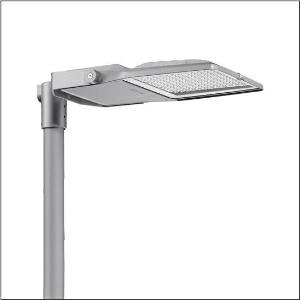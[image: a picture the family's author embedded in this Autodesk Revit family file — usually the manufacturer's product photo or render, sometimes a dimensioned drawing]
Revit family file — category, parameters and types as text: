
# Revit family: floodlight_fl_21_iq_midi___pl64_5xa7782f2e3a_4586
name_source: partatom
category: Lighting Fixtures
units: mm (PartAtom-declared; Revit-internal decimal feet)

## family parameters
Cut with Voids When Loaded = No
Host = Face
Light Source = No
Part Type = Normal
Room Calculation Point = No
Round Connector Dimension = Use Diameter
Shared = No

## types (1)
- --- (1 x LED, 34530 lm, 270.2 W, 3000K)
    Apparent Load = 270 VA
    CIE Flux Codes = 28 80 98 100 100
    Color Rendering = 70
    Color Temperature = 3000K
    Default Elevation = 1800 mm
    Description = Floodlight FL 21 iQ midi, floodlight, primary light control with lens, of PMMA, primary optical cover: protective disc, of toughened safety glass, transparent, light distribution: PL64, light emission: direct distribution, installation type: surface-mounted, LED, High Power LED, rated luminous flux: 34.530lm, luminous efficacy: 128lm/W, light colour: 730, colour temperature: 3000K, control gear: ECG iQ, control: optimised constant luminous flux control (CLO 2.0), Desk-Remote (wireless, voltage-free reading and setting of iQ features in the workshop via application-optimized NFC function/RFID function), Smart-Wire, Night-Set, Temp-Guard, Auto-Match, Street-Remote, with terminal, 6-pole, mains connection: 220..240V, AC, 50/60Hz, start of lifetime: 270W, end of service life: 287W, reduction: 117W, luminaire housing, of diecast aluminium, powder-coated, Siteco® metallic grey (DB 702S), corrosivity category C5 mid according to DIN EN ISO 12944, sealing non-destructively replaceable, please order mast flange separately, mast bracket, of steel, galvanised, powder-coated, Siteco® metallic grey (DB 702S), protection rating (complete): IP66, insulation class (complete): insulation class II (safety insulation), certification: CE, protection symbol: D, impact resistance: IK08, permissible operating ambient temperature: -40..+40°C, permissible operating ambient temperature for outdoor applications: -40..+50°C, standard: DIN EN 12944, LABS conformity tested according to VDMA 24364:2018-05, packaging unit: 1 piece

Light Distribution: PL64
    Height = 76 mm
    Lamp = 1 x LED
    Lamp Light Flux = 34530 lm
    Lamp Power = 270.2 W
    Lamp count = 1
    Length = 657 mm
    Luminous efficacy = 128 lm/W
    Manufacturer = Siteco
    ModVariant = No
    Model = 5XA7782F2E3A
    Number of Poles = 1
    OnlyDefault = Yes
    Power Factor = 1
    Product Name = Floodlight FL 21 iQ midi | PL64
    Product group = floodlight | pylon annexe
    ProductGroupID = 6200
    Protection Class = Protection class II
    Protection Degree = IP 66
    RLX_Detail_Level = 1
    RLX_Emergency_Light_Flux = 0 lm
    RLX_Emergency_Type = 0
    RLX_Emergency_Type_DB = No
    RlxData = <blob elided: 153677 chars, md5=05fb3988>
    Socket = socket
    Standby Power = 0 W
    System Light Flux = 34530 lm
    System Power = 270 W
    Type Comments = factory setting: luminous flux: 100 % | dim-lin: 254 | 620 mA
    Type Image = l_1007123.jpg
    URL = http://relux.com
    VarID = @adj_054963
    Voltage = 0 V
    Weight = 0.00 kg
    Width = 442 mm

## geometry (parser evidence)
native form markers: Blend x4, Sweep x12
no freeform markers — native parametric forms only
